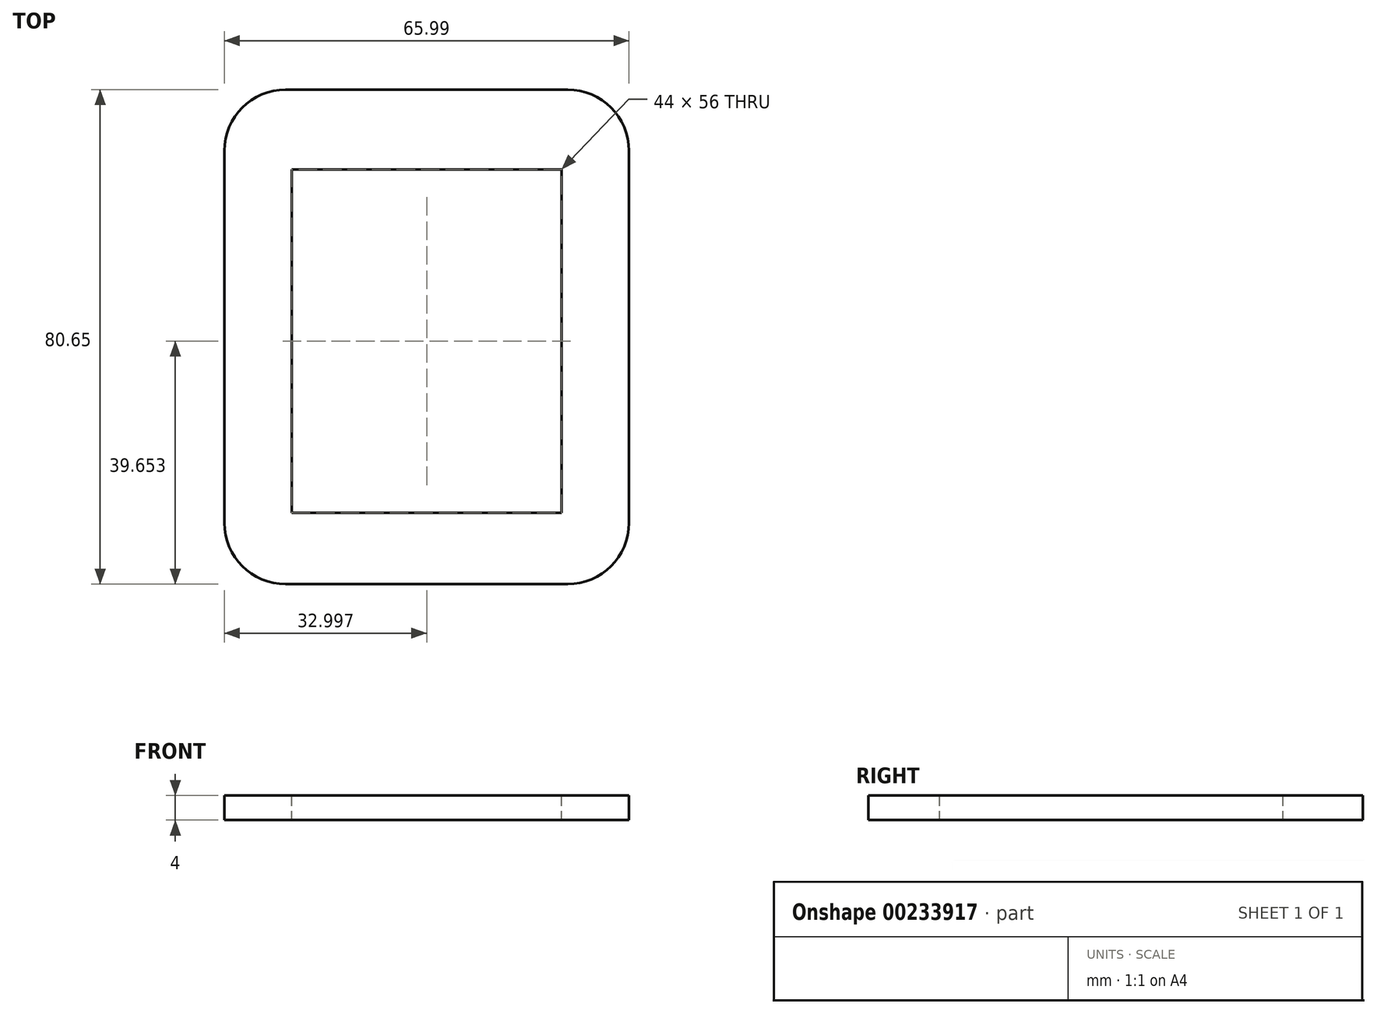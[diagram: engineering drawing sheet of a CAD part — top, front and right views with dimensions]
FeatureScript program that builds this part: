
annotation { "Feature Type Name" : "Feature", "Feature Type Description" : "" }
export const myFeature = defineFeature(function(context is Context, id is Id, definition is map)
    precondition{}
    {
        {
            var Q0;
            Q0=qCreatedBy(makeId("Top.planeOp"),FACE);
            var sketch = newSketch(context, id + "F0", { "sketchPlane" : qUnion([Q0])});
            skLineSegment(sketch, "E0.bottom", {"start": v(-32.26, 30.06) * mm, "end": v(33.73, 30.06) * mm});
            skLineSegment(sketch, "E0.top", {"start": v(-32.26, -50.6) * mm, "end": v(33.73, -50.6) * mm});
            skLineSegment(sketch, "E0.left", {"start": v(-32.26, 30.06) * mm, "end": v(-32.26, -50.6) * mm});
            skLineSegment(sketch, "E0.right", {"start": v(33.73, 30.06) * mm, "end": v(33.73, -50.6) * mm});
            skSolve(sketch);
        }
        {
            var Q0;
            Q0=makeQuery(id+"F0.imprint","IMPRINT",FACE,{"disambiguationData":[TD([[makeQuery(id+"F0.imprint","IMPRINT",EDGE,{"derivedFrom":sQuery(id+"F0.wireOp",EDGE,"E0.bottom")}),-1.0]])]});
            extrude(context, id + "F1", {"entities" : qUnion([Q0]), "depth" : 4 * mm});
        }
        {
            var Q0;
            Q0=makeQuery(id+"F1.opExtrude","CAP_FACE",FACE,{"disambiguationData":[OSD([sQuery(id+"F0.wireOp",EDGE,"E0.bottom"),sQuery(id+"F0.wireOp",EDGE,"E0.top"),sQuery(id+"F0.wireOp",EDGE,"E0.left"),sQuery(id+"F0.wireOp",EDGE,"E0.right")])],"isStart":false});
            var sketch = newSketch(context, id + "F2", { "sketchPlane" : qUnion([Q0])});
            skLineSegment(sketch, "E1.bottom", {"start": v(-21.26, 17.06) * mm, "end": v(22.74, 17.06) * mm});
            skLineSegment(sketch, "E1.top", {"start": v(-21.26, -38.94) * mm, "end": v(22.74, -38.94) * mm});
            skLineSegment(sketch, "E1.left", {"start": v(-21.26, 17.06) * mm, "end": v(-21.26, -38.94) * mm});
            skLineSegment(sketch, "E1.right", {"start": v(22.74, 17.06) * mm, "end": v(22.74, -38.94) * mm});
            skLineSegment(sketch, "E2.bottom", {"start": v(7.36, -38.94) * mm, "end": v(-8.94, -38.94) * mm});
            skLineSegment(sketch, "E2.top", {"start": v(7.36, -44.36) * mm, "end": v(-8.94, -44.36) * mm});
            skLineSegment(sketch, "E2.left", {"start": v(7.36, -38.94) * mm, "end": v(7.36, -44.36) * mm});
            skLineSegment(sketch, "E2.right", {"start": v(-8.94, -38.94) * mm, "end": v(-8.94, -44.36) * mm});
            skSolve(sketch);
        }
        {
            var Q0;
            Q0=makeQuery(id+"F1.opExtrude","SWEPT_EDGE",EDGE,{"disambiguationData":[OSD([sQuery(id+"F0.wireOp",EDGE,"E0.bottom"),sQuery(id+"F0.wireOp",EDGE,"E0.right")])]});
            var Q1;
            Q1=makeQuery(id+"F1.opExtrude","SWEPT_EDGE",EDGE,{"disambiguationData":[OSD([sQuery(id+"F0.wireOp",EDGE,"E0.bottom"),sQuery(id+"F0.wireOp",EDGE,"E0.left")])]});
            var Q2;
            Q2=makeQuery(id+"F1.opExtrude","SWEPT_EDGE",EDGE,{"disambiguationData":[OSD([sQuery(id+"F0.wireOp",EDGE,"E0.top"),sQuery(id+"F0.wireOp",EDGE,"E0.left")])]});
            var Q3;
            Q3=makeQuery(id+"F1.opExtrude","SWEPT_EDGE",EDGE,{"disambiguationData":[OSD([sQuery(id+"F0.wireOp",EDGE,"E0.top"),sQuery(id+"F0.wireOp",EDGE,"E0.right")])]});
            fillet(context, id + "F3", {"entities" : qUnion([Q0, Q1, Q2, Q3]), "radius" : 10 * mm, "tangentPropagation" : true, "allowEdgeOverflow" : false});
        }
        {
            var Q0;
            Q0=makeQuery(id+"F2.imprint","IMPRINT",FACE,{"disambiguationData":[TD([[makeQuery(id+"F2.imprint","IMPRINT",EDGE,{"derivedFrom":sQuery(id+"F2.wireOp",EDGE,"E2.bottom")}),1.0]])]});
            var Q1;
            Q1=makeQuery(id+"F2.imprint","IMPRINT",FACE,{"disambiguationData":[TD([[makeQuery(id+"F2.imprint","IMPRINT",EDGE,{"derivedFrom":sQuery(id+"F2.wireOp",EDGE,"E1.bottom")}),-1.0]])]});
            extrude(context, id + "F4", {"entities" : qUnion([Q0, Q1]), "operationType" : NewBodyOperationType.REMOVE, "oppositeDirection" : true, "depth" : 25 * mm});
        }
    });
